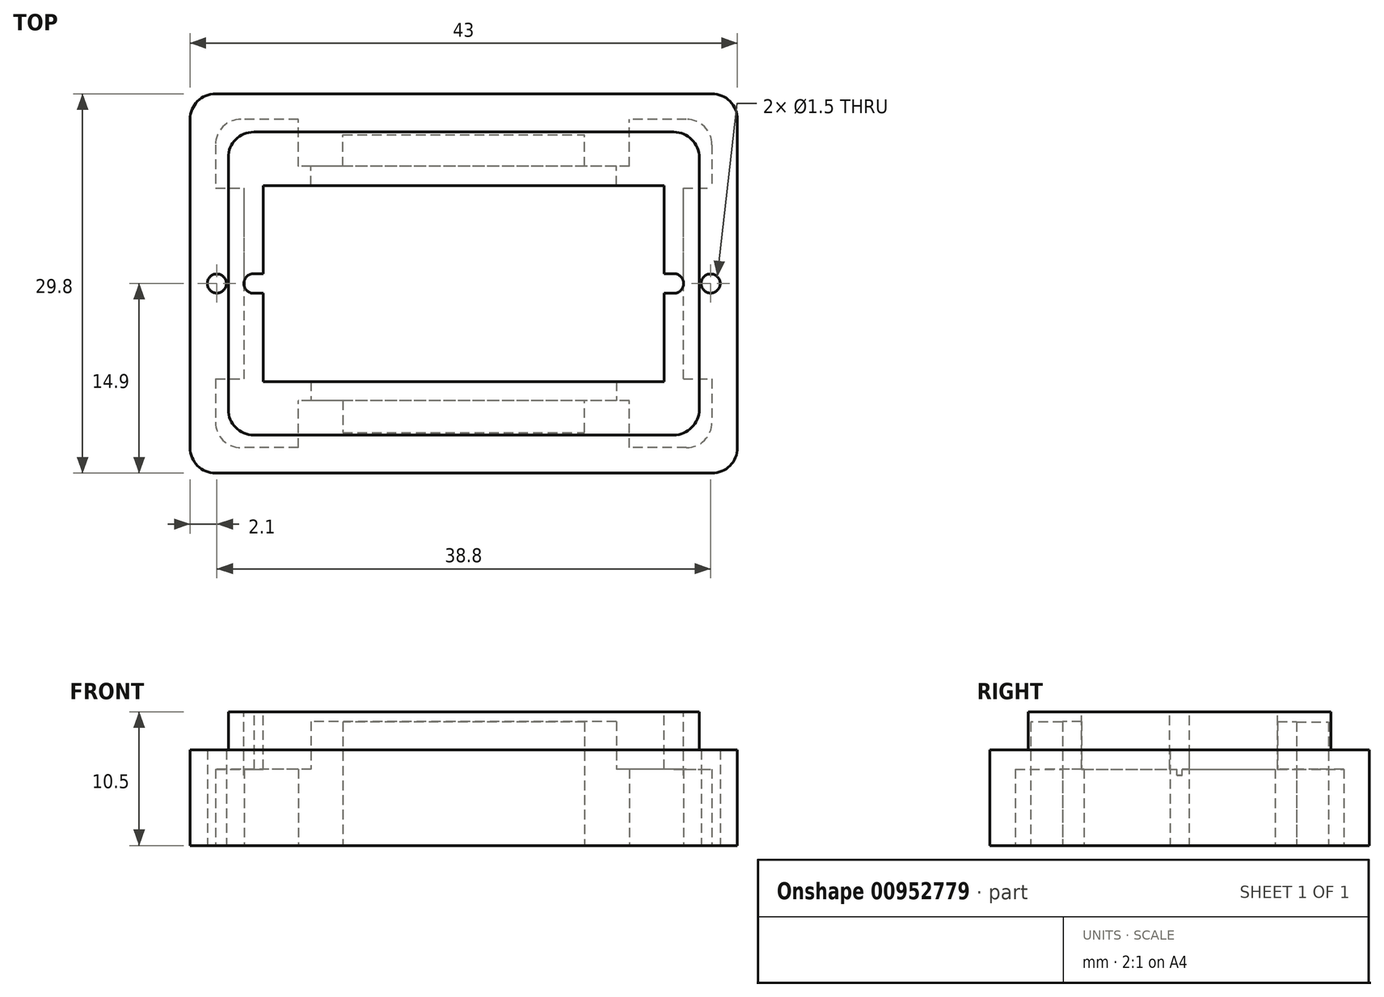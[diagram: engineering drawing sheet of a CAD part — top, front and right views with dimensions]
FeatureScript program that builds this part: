
annotation { "Feature Type Name" : "Feature", "Feature Type Description" : "" }
export const myFeature = defineFeature(function(context is Context, id is Id, definition is map)
    precondition{}
    {
        {
            var Q0;
            Q0=qCreatedBy(makeId("Top.planeOp"),FACE);
            var sketch = newSketch(context, id + "F0", { "sketchPlane" : qUnion([Q0])});
            skLineSegment(sketch, "E0.bottom", {"start": v(19.5, -14.9) * mm, "end": v(-19.5, -14.9) * mm});
            skLineSegment(sketch, "E0.top", {"start": v(19.5, 14.9) * mm, "end": v(-19.5, 14.9) * mm});
            skLineSegment(sketch, "E0.left", {"start": v(21.5, -12.9) * mm, "end": v(21.5, 12.9) * mm});
            skLineSegment(sketch, "E0.right", {"start": v(-21.5, -12.9) * mm, "end": v(-21.5, 12.9) * mm});
            skPoint(sketch, "E0.middle", {"position": v(0, 0) * mm});
            skPoint(sketch, "E1.visualSharp", {"position": v(-21.5, 14.9) * mm});
            skArc(sketch, "E1.filletArc", {"start": v(-19.5, 14.9) * mm, "mid": v(-20.91, 14.31) * mm, "end": v(-21.5, 12.9) * mm});
            skPoint(sketch, "E2.visualSharp", {"position": v(-21.5, -14.9) * mm});
            skArc(sketch, "E2.filletArc", {"start": v(-21.5, -12.9) * mm, "mid": v(-20.91, -14.31) * mm, "end": v(-19.5, -14.9) * mm});
            skPoint(sketch, "E3.visualSharp", {"position": v(21.5, 14.9) * mm});
            skArc(sketch, "E3.filletArc", {"start": v(21.5, 12.9) * mm, "mid": v(20.91, 14.31) * mm, "end": v(19.5, 14.9) * mm});
            skPoint(sketch, "E4.visualSharp", {"position": v(21.5, -14.9) * mm});
            skArc(sketch, "E4.filletArc", {"start": v(19.5, -14.9) * mm, "mid": v(20.91, -14.31) * mm, "end": v(21.5, -12.9) * mm});
            skSolve(sketch);
        }
        {
            var Q0;
            Q0 = qSketchRegion(id + "F0", true);
            extrude(context, id + "F1", {"entities" : qUnion([Q0]), "depth" : 7.5 * mm, "offsetDistance" : 25 * mm});
        }
        {
            var Q0;
            Q0=qCreatedBy(makeId("Top.planeOp"),FACE);
            var sketch = newSketch(context, id + "F2", { "sketchPlane" : qUnion([Q0])});
            skLineSegment(sketch, "E5.bottom", {"start": v(13, -9.2) * mm, "end": v(-13, -9.2) * mm});
            skLineSegment(sketch, "E5.top", {"start": v(13, 9.2) * mm, "end": v(-13, 9.2) * mm});
            skLineSegment(sketch, "E5.left", {"start": v(17.25, -7.5) * mm, "end": v(17.25, 7.5) * mm});
            skLineSegment(sketch, "E5.right", {"start": v(-17.25, -7.5) * mm, "end": v(-17.25, 7.5) * mm});
            skPoint(sketch, "E5.middle", {"position": v(0, 0) * mm});
            skLineSegment(sketch, "E6.bottom", {"start": v(17.5, 12.9) * mm, "end": v(13, 12.9) * mm});
            skLineSegment(sketch, "E6.top", {"start": v(17.5, -12.9) * mm, "end": v(13, -12.9) * mm});
            skLineSegment(sketch, "E6.left", {"start": v(19.5, 10.9) * mm, "end": v(19.5, 7.5) * mm});
            skLineSegment(sketch, "E6.right", {"start": v(-19.5, 10.9) * mm, "end": v(-19.5, 7.5) * mm});
            skPoint(sketch, "E7.visualSharp", {"position": v(-19.5, -12.9) * mm});
            skArc(sketch, "E7.filletArc", {"start": v(-19.5, -10.9) * mm, "mid": v(-18.91, -12.31) * mm, "end": v(-17.5, -12.9) * mm});
            skPoint(sketch, "E8.visualSharp", {"position": v(19.5, -12.9) * mm});
            skArc(sketch, "E8.filletArc", {"start": v(17.5, -12.9) * mm, "mid": v(18.91, -12.31) * mm, "end": v(19.5, -10.9) * mm});
            skPoint(sketch, "E9.visualSharp", {"position": v(19.5, 12.9) * mm});
            skArc(sketch, "E9.filletArc", {"start": v(19.5, 10.9) * mm, "mid": v(18.91, 12.31) * mm, "end": v(17.5, 12.9) * mm});
            skPoint(sketch, "E10.visualSharp", {"position": v(-19.5, 12.9) * mm});
            skArc(sketch, "E10.filletArc", {"start": v(-17.5, 12.9) * mm, "mid": v(-18.91, 12.31) * mm, "end": v(-19.5, 10.9) * mm});
            skLineSegment(sketch, "E11", {"start": v(-13, -12.9) * mm, "end": v(-13, -9.2) * mm});
            skLineSegment(sketch, "E12", {"start": v(13, -12.9) * mm, "end": v(13, -9.2) * mm});
            skLineSegment(sketch, "E13", {"start": v(-13, 9.2) * mm, "end": v(-13, 12.9) * mm});
            skLineSegment(sketch, "E14", {"start": v(13, 9.2) * mm, "end": v(13, 12.9) * mm});
            skLineSegment(sketch, "E15", {"start": v(-19.5, -7.5) * mm, "end": v(-17.25, -7.5) * mm});
            skLineSegment(sketch, "E16", {"start": v(-19.5, 7.5) * mm, "end": v(-17.25, 7.5) * mm});
            skLineSegment(sketch, "E17", {"start": v(17.25, -7.5) * mm, "end": v(19.5, -7.5) * mm});
            skLineSegment(sketch, "E18", {"start": v(17.25, 7.5) * mm, "end": v(19.5, 7.5) * mm});
            skPoint(sketch, "E19.orphan", {"position": v(-17.25, -9.2) * mm});
            skLineSegment(sketch, "E20.trimOffspring", {"start": v(-19.5, -7.5) * mm, "end": v(-19.5, -10.9) * mm});
            skPoint(sketch, "E21.orphan", {"position": v(-17.25, 9.2) * mm});
            skLineSegment(sketch, "E22.trimOffspring", {"start": v(-13, 12.9) * mm, "end": v(-17.5, 12.9) * mm});
            skPoint(sketch, "E23.orphan", {"position": v(17.25, 9.2) * mm});
            skLineSegment(sketch, "E24.trimOffspring", {"start": v(19.5, -7.5) * mm, "end": v(19.5, -10.9) * mm});
            skPoint(sketch, "E25.orphan", {"position": v(17.25, -9.2) * mm});
            skLineSegment(sketch, "E26.trimOffspring", {"start": v(-13, -12.9) * mm, "end": v(-17.5, -12.9) * mm});
            skSolve(sketch);
        }
        {
            var Q0;
            Q0 = qSketchRegion(id + "F2", true);
            extrude(context, id + "F3", {"entities" : qUnion([Q0]), "operationType" : NewBodyOperationType.REMOVE, "depth" : 6 * mm, "offsetDistance" : 25 * mm});
        }
        {
            var Q0;
            Q0=makeQuery(id+"F1.opExtrude","CAP_FACE",FACE,{"disambiguationData":[OSD([sQuery(id+"F0.wireOp",EDGE,"E0.bottom"),sQuery(id+"F0.wireOp",EDGE,"E0.top"),sQuery(id+"F0.wireOp",EDGE,"E0.left"),sQuery(id+"F0.wireOp",EDGE,"E0.right"),sQuery(id+"F0.wireOp",EDGE,"E1.filletArc"),sQuery(id+"F0.wireOp",EDGE,"E2.filletArc"),sQuery(id+"F0.wireOp",EDGE,"E3.filletArc"),sQuery(id+"F0.wireOp",EDGE,"E4.filletArc")])],"isStart":false});
            var sketch = newSketch(context, id + "F4", { "sketchPlane" : qUnion([Q0])});
            skLineSegment(sketch, "E27.bottom", {"start": v(16.5, -11.9) * mm, "end": v(-16.5, -11.9) * mm});
            skLineSegment(sketch, "E27.top", {"start": v(16.5, 11.9) * mm, "end": v(-16.5, 11.9) * mm});
            skLineSegment(sketch, "E27.left", {"start": v(18.5, -9.9) * mm, "end": v(18.5, 9.9) * mm});
            skLineSegment(sketch, "E27.right", {"start": v(-18.5, -9.9) * mm, "end": v(-18.5, 9.9) * mm});
            skPoint(sketch, "E27.middle", {"position": v(0, 0) * mm});
            skPoint(sketch, "E28.visualSharp", {"position": v(-18.5, 11.9) * mm});
            skArc(sketch, "E28.filletArc", {"start": v(-16.5, 11.9) * mm, "mid": v(-17.91, 11.31) * mm, "end": v(-18.5, 9.9) * mm});
            skPoint(sketch, "E29.visualSharp", {"position": v(-18.5, -11.9) * mm});
            skArc(sketch, "E29.filletArc", {"start": v(-18.5, -9.9) * mm, "mid": v(-17.91, -11.31) * mm, "end": v(-16.5, -11.9) * mm});
            skPoint(sketch, "E30.visualSharp", {"position": v(18.5, 11.9) * mm});
            skArc(sketch, "E30.filletArc", {"start": v(18.5, 9.9) * mm, "mid": v(17.91, 11.31) * mm, "end": v(16.5, 11.9) * mm});
            skPoint(sketch, "E31.visualSharp", {"position": v(18.5, -11.9) * mm});
            skArc(sketch, "E31.filletArc", {"start": v(16.5, -11.9) * mm, "mid": v(17.91, -11.31) * mm, "end": v(18.5, -9.9) * mm});
            skSolve(sketch);
        }
        {
            var Q0;
            Q0 = qSketchRegion(id + "F4", true);
            extrude(context, id + "F5", {"entities" : qUnion([Q0]), "operationType" : NewBodyOperationType.ADD, "depth" : 3 * mm, "offsetDistance" : 25 * mm});
        }
        {
            var Q0;
            Q0=makeQuery(id+"F5.opExtrude","CAP_FACE",FACE,{"disambiguationData":[OSD([sQuery(id+"F4.wireOp",EDGE,"E27.bottom"),sQuery(id+"F4.wireOp",EDGE,"E27.top"),sQuery(id+"F4.wireOp",EDGE,"E27.left"),sQuery(id+"F4.wireOp",EDGE,"E27.right"),sQuery(id+"F4.wireOp",EDGE,"E28.filletArc"),sQuery(id+"F4.wireOp",EDGE,"E29.filletArc"),sQuery(id+"F4.wireOp",EDGE,"E30.filletArc"),sQuery(id+"F4.wireOp",EDGE,"E31.filletArc")])],"isStart":false});
            var sketch = newSketch(context, id + "F6", { "sketchPlane" : qUnion([Q0])});
            skLineSegment(sketch, "E32.bottom", {"start": v(15.75, -7.7) * mm, "end": v(-15.75, -7.7) * mm});
            skLineSegment(sketch, "E32.top", {"start": v(15.75, 7.7) * mm, "end": v(-15.75, 7.7) * mm});
            skLineSegment(sketch, "E32.left", {"start": v(15.75, -7.7) * mm, "end": v(15.75, -0.77) * mm});
            skLineSegment(sketch, "E32.right", {"start": v(-15.75, -7.7) * mm, "end": v(-15.75, -0.77) * mm});
            skPoint(sketch, "E32.middle", {"position": v(0, 0) * mm});
            skArc(sketch, "E33", {"start": v(-16.46, 0.77) * mm, "mid": v(-17.27, 0.02) * mm, "end": v(-16.5, -0.78) * mm});
            skArc(sketch, "E34", {"start": v(16.5, -0.77) * mm, "mid": v(17.27, 0) * mm, "end": v(16.5, 0.78) * mm});
            skLineSegment(sketch, "E35", {"start": v(-16.46, 0.77) * mm, "end": v(-15.75, 0.77) * mm});
            skLineSegment(sketch, "E36", {"start": v(-16.5, -0.78) * mm, "end": v(-15.75, -0.77) * mm});
            skLineSegment(sketch, "E37.trimOffspring", {"start": v(-15.75, 0.77) * mm, "end": v(-15.75, 7.7) * mm});
            skLineSegment(sketch, "E38", {"start": v(16.5, 0.78) * mm, "end": v(15.75, 0.77) * mm});
            skLineSegment(sketch, "E39", {"start": v(16.5, -0.77) * mm, "end": v(15.75, -0.77) * mm});
            skLineSegment(sketch, "E40.trimOffspring", {"start": v(15.75, 0.78) * mm, "end": v(15.75, 7.7) * mm});
            skSolve(sketch);
        }
        {
            var Q0;
            Q0 = qSketchRegion(id + "F6", true);
            extrude(context, id + "F7", {"entities" : qUnion([Q0]), "operationType" : NewBodyOperationType.REMOVE, "oppositeDirection" : true, "depth" : 5 * mm, "offsetDistance" : 25 * mm});
        }
        {
            var Q0;
            {var subQ0=sQuery(id+"F2.wireOp",EDGE,"E10.filletArc");var subQ1=sQuery(id+"F2.wireOp",EDGE,"E9.filletArc");var subQ2=sQuery(id+"F2.wireOp",EDGE,"E6.right");var subQ3=sQuery(id+"F2.wireOp",EDGE,"E6.left");var subQ5=sQuery(id+"F2.wireOp",EDGE,"E5.top");var subQ7=sQuery(id+"F2.wireOp",EDGE,"E5.left");var subQ8=sQuery(id+"F2.wireOp",EDGE,"E13");var subQ9=sQuery(id+"F2.wireOp",EDGE,"E5.right");var subQ11=sQuery(id+"F2.wireOp",EDGE,"E14");var subQ12=sQuery(id+"F2.wireOp",EDGE,"E6.bottom");var subQ14=sQuery(id+"F2.wireOp",EDGE,"E16");var subQ15=sQuery(id+"F2.wireOp",EDGE,"E18");var subQ17=sQuery(id+"F2.wireOp",EDGE,"E22.trimOffspring");Q0=makeQuery(id+"F7.boolean.opBoolean","SPLIT",FACE,{"disambiguationData":[TD([makeQuery(id+"F3.boolean.opBoolean","COPY",FACE,{"derivedFrom":makeQuery(id+"F3.opExtrude","SWEPT_FACE",FACE,{"disambiguationData":[OSD([subQ5])]})})])],"derivedFrom":makeQuery(id+"F3.boolean.opBoolean","COPY",FACE,{"derivedFrom":makeQuery(id+"F3.opExtrude","CAP_FACE",FACE,{"disambiguationData":[OSD([sQuery(id+"F2.wireOp",EDGE,"E5.bottom"),subQ5,subQ7,subQ9,subQ12,sQuery(id+"F2.wireOp",EDGE,"E6.top"),subQ3,subQ2,sQuery(id+"F2.wireOp",EDGE,"E7.filletArc"),sQuery(id+"F2.wireOp",EDGE,"E8.filletArc"),subQ1,subQ0,sQuery(id+"F2.wireOp",EDGE,"E11"),sQuery(id+"F2.wireOp",EDGE,"E12"),subQ8,subQ11,sQuery(id+"F2.wireOp",EDGE,"E15"),subQ14,sQuery(id+"F2.wireOp",EDGE,"E17"),subQ15,sQuery(id+"F2.wireOp",EDGE,"E20.trimOffspring"),subQ17,sQuery(id+"F2.wireOp",EDGE,"E24.trimOffspring"),sQuery(id+"F2.wireOp",EDGE,"E26.trimOffspring")])],"isStart":false})})});}
            var sketch = newSketch(context, id + "F8", { "sketchPlane" : qUnion([Q0])});
            skLineSegment(sketch, "E41.bottom", {"start": v(-12, -7.7) * mm, "end": v(12, -7.7) * mm});
            skLineSegment(sketch, "E41.top", {"start": v(-12, -9.2) * mm, "end": v(12, -9.2) * mm});
            skLineSegment(sketch, "E41.left", {"start": v(-12, -7.7) * mm, "end": v(-12, -9.2) * mm});
            skLineSegment(sketch, "E41.right", {"start": v(12, -7.7) * mm, "end": v(12, -9.2) * mm});
            skLineSegment(sketch, "E42", {"start": v(-12, 9.2) * mm, "end": v(-12, 7.72) * mm});
            skLineSegment(sketch, "E43", {"start": v(12, 9.27) * mm, "end": v(12, 7.72) * mm});
            skSolve(sketch);
        }
        {
            var Q0;
            Q0 = qSketchRegion(id + "F8", true);
            extrude(context, id + "F9", {"entities" : qUnion([Q0]), "operationType" : NewBodyOperationType.REMOVE, "oppositeDirection" : true, "depth" : 3.75 * mm, "offsetDistance" : 25 * mm});
        }
        {
            var Q0;
            Q0=makeQuery(id+"F1.opExtrude","CAP_FACE",FACE,{"disambiguationData":[OSD([sQuery(id+"F0.wireOp",EDGE,"E0.bottom"),sQuery(id+"F0.wireOp",EDGE,"E0.top"),sQuery(id+"F0.wireOp",EDGE,"E0.left"),sQuery(id+"F0.wireOp",EDGE,"E0.right"),sQuery(id+"F0.wireOp",EDGE,"E1.filletArc"),sQuery(id+"F0.wireOp",EDGE,"E2.filletArc"),sQuery(id+"F0.wireOp",EDGE,"E3.filletArc"),sQuery(id+"F0.wireOp",EDGE,"E4.filletArc")])],"isStart":true});
            var sketch = newSketch(context, id + "F10", { "sketchPlane" : qUnion([Q0])});
            skLineSegment(sketch, "E44.bottom", {"start": v(-9.5, -9.2) * mm, "end": v(9.5, -9.2) * mm});
            skLineSegment(sketch, "E44.top", {"start": v(-9.5, -11.7) * mm, "end": v(9.5, -11.7) * mm});
            skLineSegment(sketch, "E44.left", {"start": v(-9.5, -9.2) * mm, "end": v(-9.5, -11.7) * mm});
            skLineSegment(sketch, "E44.right", {"start": v(9.5, -9.2) * mm, "end": v(9.5, -11.7) * mm});
            skLineSegment(sketch, "E45", {"start": v(-9.5, 9.2) * mm, "end": v(-9.5, 11.7) * mm});
            skPoint(sketch, "E45.endSnap0", {"position": v(-13, 11.7) * mm});
            skLineSegment(sketch, "E46", {"start": v(-9.5, 11.7) * mm, "end": v(9.5, 11.7) * mm});
            skLineSegment(sketch, "E47", {"start": v(9.5, 11.7) * mm, "end": v(9.5, 9.2) * mm});
            skSolve(sketch);
        }
        {
            var Q0;
            Q0 = qSketchRegion(id + "F10", true);
            extrude(context, id + "F11", {"entities" : qUnion([Q0]), "operationType" : NewBodyOperationType.REMOVE, "oppositeDirection" : true, "depth" : 9.7 * mm, "offsetDistance" : 25 * mm});
        }
        {
            var Q0;
            Q0=makeQuery(id+"F1.opExtrude","CAP_FACE",FACE,{"disambiguationData":[OSD([sQuery(id+"F0.wireOp",EDGE,"E0.bottom"),sQuery(id+"F0.wireOp",EDGE,"E0.top"),sQuery(id+"F0.wireOp",EDGE,"E0.left"),sQuery(id+"F0.wireOp",EDGE,"E0.right"),sQuery(id+"F0.wireOp",EDGE,"E1.filletArc"),sQuery(id+"F0.wireOp",EDGE,"E2.filletArc"),sQuery(id+"F0.wireOp",EDGE,"E3.filletArc"),sQuery(id+"F0.wireOp",EDGE,"E4.filletArc")])],"isStart":true});
            var sketch = newSketch(context, id + "F12", { "sketchPlane" : qUnion([Q0])});
            skCircle(sketch, "E48", {"center": v(19.4, 0) * mm, "radius": 0.75 * mm});
            skCircle(sketch, "E49", {"center": v(-19.4, 0) * mm, "radius": 0.75 * mm});
            skSolve(sketch);
        }
        {
            var Q0;
            Q0 = qSketchRegion(id + "F12", true);
            extrude(context, id + "F13", {"entities" : qUnion([Q0]), "operationType" : NewBodyOperationType.REMOVE, "oppositeDirection" : true, "depth" : 7.7 * mm, "offsetDistance" : 25 * mm});
        }
        {
            var Q0;
            {var subQ0=sQuery(id+"F2.wireOp",EDGE,"E11");var subQ1=sQuery(id+"F2.wireOp",EDGE,"E8.filletArc");var subQ2=sQuery(id+"F2.wireOp",EDGE,"E7.filletArc");var subQ3=sQuery(id+"F2.wireOp",EDGE,"E15");var subQ4=sQuery(id+"F2.wireOp",EDGE,"E6.top");var subQ5=sQuery(id+"F2.wireOp",EDGE,"E5.bottom");var subQ6=sQuery(id+"F2.wireOp",EDGE,"E24.trimOffspring");var subQ7=sQuery(id+"F2.wireOp",EDGE,"E26.trimOffspring");var subQ8=sQuery(id+"F2.wireOp",EDGE,"E20.trimOffspring");var subQ9=sQuery(id+"F2.wireOp",EDGE,"E17");var subQ10=sQuery(id+"F2.wireOp",EDGE,"E12");var subQ11=sQuery(id+"F2.wireOp",EDGE,"E5.right");var subQ12=sQuery(id+"F2.wireOp",EDGE,"E5.left");var subQ13=makeQuery(id+"F3.boolean.opBoolean","COPY",FACE,{"derivedFrom":makeQuery(id+"F3.opExtrude","CAP_FACE",FACE,{"disambiguationData":[OSD([subQ5,sQuery(id+"F2.wireOp",EDGE,"E5.top"),subQ12,subQ11,sQuery(id+"F2.wireOp",EDGE,"E6.bottom"),subQ4,sQuery(id+"F2.wireOp",EDGE,"E6.left"),sQuery(id+"F2.wireOp",EDGE,"E6.right"),subQ2,subQ1,sQuery(id+"F2.wireOp",EDGE,"E9.filletArc"),sQuery(id+"F2.wireOp",EDGE,"E10.filletArc"),subQ0,subQ10,sQuery(id+"F2.wireOp",EDGE,"E13"),sQuery(id+"F2.wireOp",EDGE,"E14"),subQ3,sQuery(id+"F2.wireOp",EDGE,"E16"),subQ9,sQuery(id+"F2.wireOp",EDGE,"E18"),subQ8,sQuery(id+"F2.wireOp",EDGE,"E22.trimOffspring"),subQ6,subQ7])],"isStart":false})});Q0=makeQuery(id+"F7.boolean.opBoolean","SPLIT",FACE,{"disambiguationData":[TD([makeQuery(id+"F3.boolean.opBoolean","COPY",FACE,{"derivedFrom":makeQuery(id+"F3.opExtrude","SWEPT_FACE",FACE,{"disambiguationData":[OSD([subQ5])]})})])],"derivedFrom":subQ13});}
            var sketch = newSketch(context, id + "F14", { "sketchPlane" : qUnion([Q0])});
            skLineSegment(sketch, "E50.bottom", {"start": v(12, 7.7) * mm, "end": v(-12, 7.7) * mm});
            skLineSegment(sketch, "E50.top", {"start": v(12, 9.2) * mm, "end": v(-12, 9.2) * mm});
            skLineSegment(sketch, "E50.left", {"start": v(12, 7.7) * mm, "end": v(12, 9.2) * mm});
            skLineSegment(sketch, "E50.right", {"start": v(-12, 7.7) * mm, "end": v(-12, 9.2) * mm});
            skPoint(sketch, "E50.middle", {"position": v(0, 8.45) * mm});
            skPoint(sketch, "E50.middle.positionSnap0", {"position": v(0, 7.7) * mm});
            skPoint(sketch, "E50.centerSnap0", {"position": v(0, 7.7) * mm});
            skSolve(sketch);
        }
        {
            var Q0;
            Q0 = qSketchRegion(id + "F14", true);
            extrude(context, id + "F15", {"entities" : qUnion([Q0]), "operationType" : NewBodyOperationType.REMOVE, "oppositeDirection" : true, "depth" : 3.75 * mm, "offsetDistance" : 25 * mm});
        }
        {
            var Q0;
            {var subQ0=sQuery(id+"F10.wireOp",EDGE,"E45");Q0=makeQuery(id+"F10.imprint","IMPRINT",FACE,{"disambiguationData":[TD([[makeQuery(id+"F10.imprint","IMPRINT",EDGE,{"derivedFrom":subQ0}),-1.0]])]});}
            extrude(context, id + "F16", {"entities" : qUnion([Q0]), "operationType" : NewBodyOperationType.REMOVE, "oppositeDirection" : true, "depth" : 9.7 * mm, "offsetDistance" : 25 * mm});
        }
    });
